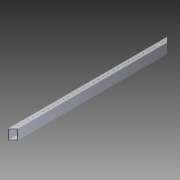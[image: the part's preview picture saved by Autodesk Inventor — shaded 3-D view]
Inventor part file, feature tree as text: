
AUTODESK INVENTOR PART (.ipt)
format: ipt  version: 2015 (Build 190159000, 159)  size: 747,520 bytes
history: native  units: in
note: dims shown in document units (in); Inventor stores cm internally (conversion verified against a paired STEP export)
features: sketch x3, other x2, extrude x2, imported_body x1
ambient origin geometry x8: Origin, YZ Plane, XZ Plane, XY Plane, X Axis, Y Axis, Z Axis, Center Point
bodies: Body1 (feature_tree)
feature tree (8):
  other  "Cut-Extrude2"
  other  "217-3453-STEP1"
  sketch  "Sketch1"  dims[d0=0.3092in d1=2.0in d2=0.0in]
  extrude  "Extrusion1"  Depth=2.0in TaperAngle=0.0deg
  extrude  "Extrusion2"  Depth=0.3092in
  imported_body  "Base1"
  sketch  "Sketch2"  dims[d3=31.667in d4=0.3092in]
  sketch  "Sketch3"  dims[d5=2.0in d6=0.0in]
